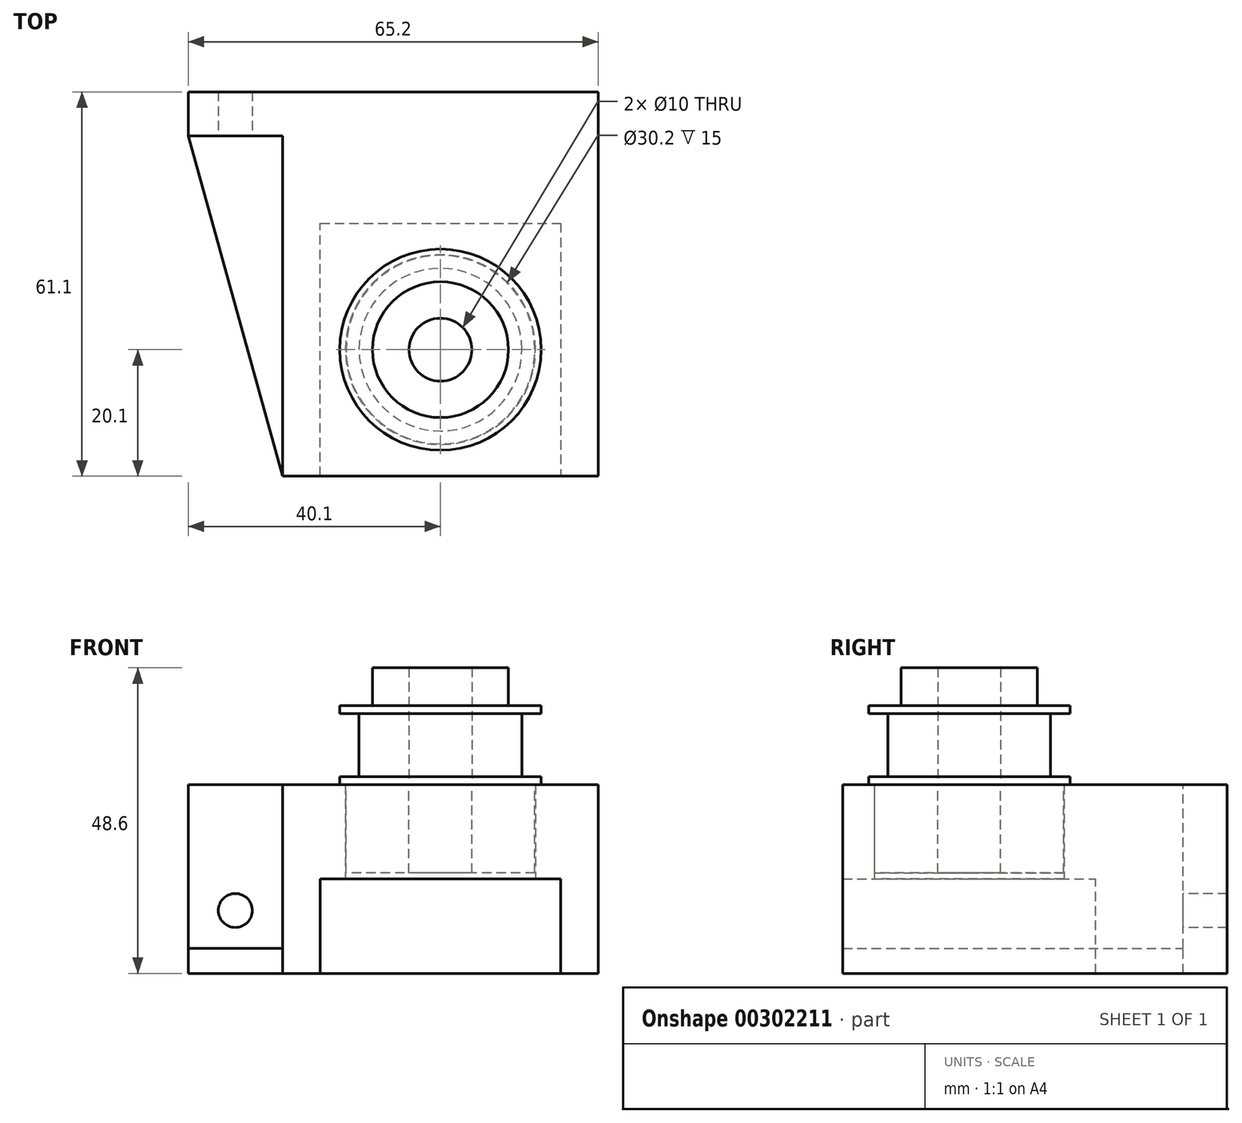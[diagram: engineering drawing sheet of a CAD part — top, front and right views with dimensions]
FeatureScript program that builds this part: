
annotation { "Feature Type Name" : "Feature", "Feature Type Description" : "" }
export const myFeature = defineFeature(function(context is Context, id is Id, definition is map)
    precondition{}
    {
        {
            var Q0;
            Q0=qCreatedBy(makeId("Top.planeOp"),FACE);
            var sketch = newSketch(context, id + "F0", { "sketchPlane" : qUnion([Q0])});
            skCircle(sketch, "E0", {"center": v(0, 0) * mm, "radius": 15.1 * mm});
            skLineSegment(sketch, "E1.bottom", {"start": v(25.1, -20.1) * mm, "end": v(-25.1, -20.1) * mm});
            skLineSegment(sketch, "E1.top", {"start": v(25.1, 41) * mm, "end": v(-25.1, 41) * mm});
            skLineSegment(sketch, "E1.left", {"start": v(25.1, -20.1) * mm, "end": v(25.1, 41) * mm});
            skLineSegment(sketch, "E1.right", {"start": v(-25.1, -20.1) * mm, "end": v(-25.1, 41) * mm});
            skPoint(sketch, "E1.middle", {"position": v(0, 10.45) * mm});
            skSolve(sketch);
        }
        {
            var Q0;
            Q0 = qSketchRegion(id + "F0", true);
            extrude(context, id + "F1", {"entities" : qUnion([Q0]), "depth" : 15 * mm});
        }
        {
            var Q0;
            Q0=makeQuery(id+"F1.opExtrude","CAP_FACE",FACE,{"disambiguationData":[OSD([sQuery(id+"F0.wireOp",EDGE,"E0"),sQuery(id+"F0.wireOp",EDGE,"E1.bottom"),sQuery(id+"F0.wireOp",EDGE,"E1.top"),sQuery(id+"F0.wireOp",EDGE,"E1.left"),sQuery(id+"F0.wireOp",EDGE,"E1.right")])],"isStart":false});
            var sketch = newSketch(context, id + "F2", { "sketchPlane" : qUnion([Q0])});
            skCircle(sketch, "E2", {"center": v(0, 0) * mm, "radius": 15 * mm});
            skCircle(sketch, "E3", {"center": v(0, 0) * mm, "radius": 5 * mm});
            skSolve(sketch);
        }
        {
            var Q0;
            Q0 = qSketchRegion(id + "F2", true);
            extrude(context, id + "F3", {"entities" : qUnion([Q0]), "oppositeDirection" : true, "depth" : 14 * mm});
        }
        {
            var Q0;
            Q0=makeQuery(id+"F1.opExtrude","CAP_FACE",FACE,{"disambiguationData":[OSD([sQuery(id+"F0.wireOp",EDGE,"E0"),sQuery(id+"F0.wireOp",EDGE,"E1.bottom"),sQuery(id+"F0.wireOp",EDGE,"E1.top"),sQuery(id+"F0.wireOp",EDGE,"E1.left"),sQuery(id+"F0.wireOp",EDGE,"E1.right")])],"isStart":true});
            var sketch = newSketch(context, id + "F4", { "sketchPlane" : qUnion([Q0])});
            skLineSegment(sketch, "E4", {"start": v(-25.1, -41) * mm, "end": v(-25.1, 20.1) * mm});
            skLineSegment(sketch, "E5", {"start": v(-25.1, 20.1) * mm, "end": v(-19.1, 20.1) * mm});
            skLineSegment(sketch, "E6", {"start": v(-19.1, 20.1) * mm, "end": v(-19.1, -20.1) * mm});
            skLineSegment(sketch, "E7", {"start": v(-19.1, -20.1) * mm, "end": v(19.1, -20.1) * mm});
            skLineSegment(sketch, "E8", {"start": v(19.1, -20.1) * mm, "end": v(19.1, 20.1) * mm});
            skLineSegment(sketch, "E9", {"start": v(19.1, 20.1) * mm, "end": v(25.1, 20.1) * mm});
            skLineSegment(sketch, "E10", {"start": v(25.1, 20.1) * mm, "end": v(25.1, -41) * mm});
            skLineSegment(sketch, "E11", {"start": v(25.1, -41) * mm, "end": v(-25.1, -41) * mm});
            skSolve(sketch);
        }
        {
            var Q0;
            Q0 = qSketchRegion(id + "F4", true);
            extrude(context, id + "F5", {"entities" : qUnion([Q0]), "operationType" : NewBodyOperationType.ADD, "depth" : 15 * mm});
        }
        {
            var Q0;
            Q0=makeQuery(id+"F5.boolean.opBoolean","MERGE",FACE,{"derivedFrom":[makeQuery(id+"F1.opExtrude","SWEPT_FACE",FACE,{"disambiguationData":[OSD([sQuery(id+"F0.wireOp",EDGE,"E1.right")])]}),makeQuery(id+"F5.opExtrude","SWEPT_FACE",FACE,{"disambiguationData":[OSD([sQuery(id+"F4.wireOp",EDGE,"E4")])]})]});
            var sketch = newSketch(context, id + "F6", { "sketchPlane" : qUnion([Q0])});
            skLineSegment(sketch, "E12.bottom", {"start": v(-41, -15) * mm, "end": v(-34, -15) * mm});
            skLineSegment(sketch, "E12.top", {"start": v(-41, 15) * mm, "end": v(-34, 15) * mm});
            skLineSegment(sketch, "E12.left", {"start": v(-41, -15) * mm, "end": v(-41, 15) * mm});
            skLineSegment(sketch, "E12.right", {"start": v(-34, -15) * mm, "end": v(-34, 15) * mm});
            skSolve(sketch);
        }
        {
            var Q0;
            Q0 = qSketchRegion(id + "F6", true);
            extrude(context, id + "F7", {"entities" : qUnion([Q0]), "operationType" : NewBodyOperationType.ADD, "depth" : 15 * mm});
        }
        {
            var Q0;
            Q0=makeQuery(id+"F7.opExtrude","SWEPT_FACE",FACE,{"disambiguationData":[OSD([sQuery(id+"F6.wireOp",EDGE,"E12.right")])]});
            var sketch = newSketch(context, id + "F8", { "sketchPlane" : qUnion([Q0])});
            skLineSegment(sketch, "E13", {"start": v(-32.6, 15) * mm, "end": v(-32.6, -15) * mm, "construction": true});
            skCircle(sketch, "E14", {"center": v(-32.6, -5) * mm, "radius": 2.7 * mm});
            skSolve(sketch);
        }
        {
            var Q0;
            Q0 = qSketchRegion(id + "F8", true);
            extrude(context, id + "F9", {"entities" : qUnion([Q0]), "operationType" : NewBodyOperationType.REMOVE, "oppositeDirection" : true, "depth" : 25 * mm});
        }
        {
            var Q0;
            Q0=makeQuery(id+"F7.boolean.opBoolean","MERGE",FACE,{"derivedFrom":[makeQuery(id+"F5.opExtrude","CAP_FACE",FACE,{"disambiguationData":[OSD([sQuery(id+"F4.wireOp",EDGE,"E4"),sQuery(id+"F4.wireOp",EDGE,"E5"),sQuery(id+"F4.wireOp",EDGE,"E6"),sQuery(id+"F4.wireOp",EDGE,"E7"),sQuery(id+"F4.wireOp",EDGE,"E8"),sQuery(id+"F4.wireOp",EDGE,"E9"),sQuery(id+"F4.wireOp",EDGE,"E10"),sQuery(id+"F4.wireOp",EDGE,"E11")])],"isStart":false}),makeQuery(id+"F7.opExtrude","SWEPT_FACE",FACE,{"disambiguationData":[OSD([sQuery(id+"F6.wireOp",EDGE,"E12.bottom")])]})]});
            var sketch = newSketch(context, id + "F10", { "sketchPlane" : qUnion([Q0])});
            skLineSegment(sketch, "E15", {"start": v(-25.1, 20.1) * mm, "end": v(-25.1, -34) * mm});
            skLineSegment(sketch, "E16", {"start": v(-25.1, -34) * mm, "end": v(-40.1, -34) * mm});
            skLineSegment(sketch, "E17", {"start": v(-40.1, -34) * mm, "end": v(-25.1, 20.1) * mm});
            skSolve(sketch);
        }
        {
            var Q0;
            Q0 = qSketchRegion(id + "F10", true);
            extrude(context, id + "F11", {"entities" : qUnion([Q0]), "operationType" : NewBodyOperationType.ADD, "oppositeDirection" : true, "depth" : 4 * mm});
        }
        {
            var Q0;
            Q0=makeQuery(id+"F3.opExtrude","CAP_FACE",FACE,{"disambiguationData":[OSD([sQuery(id+"F2.wireOp",EDGE,"E2"),sQuery(id+"F2.wireOp",EDGE,"E3")])],"isStart":true});
            var sketch = newSketch(context, id + "F12", { "sketchPlane" : qUnion([Q0])});
            skCircle(sketch, "E18", {"center": v(0, 0) * mm, "radius": 5 * mm});
            skCircle(sketch, "E19", {"center": v(0, 0) * mm, "radius": 16 * mm});
            skSolve(sketch);
        }
        {
            var Q0;
            Q0 = qSketchRegion(id + "F12", true);
            extrude(context, id + "F13", {"entities" : qUnion([Q0]), "depth" : 1.3 * mm});
        }
        {
            var Q0;
            Q0=makeQuery(id+"F13.opExtrude","CAP_FACE",FACE,{"disambiguationData":[OSD([sQuery(id+"F12.wireOp",EDGE,"E18"),sQuery(id+"F12.wireOp",EDGE,"E19")])],"isStart":false});
            var sketch = newSketch(context, id + "F14", { "sketchPlane" : qUnion([Q0])});
            skCircle(sketch, "E20", {"center": v(0, 0) * mm, "radius": 5 * mm});
            skCircle(sketch, "E21", {"center": v(0, 0) * mm, "radius": 12.94 * mm});
            skSolve(sketch);
        }
        {
            var Q0;
            Q0 = qSketchRegion(id + "F14", true);
            extrude(context, id + "F15", {"entities" : qUnion([Q0]), "operationType" : NewBodyOperationType.ADD, "depth" : 10 * mm});
        }
        {
            var Q0;
            Q0=makeQuery(id+"F15.opExtrude","CAP_FACE",FACE,{"disambiguationData":[OSD([sQuery(id+"F14.wireOp",EDGE,"E20"),sQuery(id+"F14.wireOp",EDGE,"E21")])],"isStart":false});
            var sketch = newSketch(context, id + "F16", { "sketchPlane" : qUnion([Q0])});
            skCircle(sketch, "E22", {"center": v(0, 0) * mm, "radius": 5 * mm});
            skCircle(sketch, "E23", {"center": v(0, 0) * mm, "radius": 16 * mm});
            skSolve(sketch);
        }
        {
            var Q0;
            Q0 = qSketchRegion(id + "F16", true);
            extrude(context, id + "F17", {"entities" : qUnion([Q0]), "operationType" : NewBodyOperationType.ADD, "depth" : 1.3 * mm});
        }
        {
            var Q0;
            Q0=makeQuery(id+"F17.opExtrude","CAP_FACE",FACE,{"disambiguationData":[OSD([sQuery(id+"F16.wireOp",EDGE,"E22"),sQuery(id+"F16.wireOp",EDGE,"E23")])],"isStart":false});
            var sketch = newSketch(context, id + "F18", { "sketchPlane" : qUnion([Q0])});
            skCircle(sketch, "E24", {"center": v(0, 0) * mm, "radius": 5 * mm});
            skCircle(sketch, "E25", {"center": v(0, 0) * mm, "radius": 10.8 * mm});
            skSolve(sketch);
        }
        {
            var Q0;
            Q0 = qSketchRegion(id + "F18", true);
            extrude(context, id + "F19", {"entities" : qUnion([Q0]), "operationType" : NewBodyOperationType.ADD, "depth" : 6 * mm});
        }
    });
